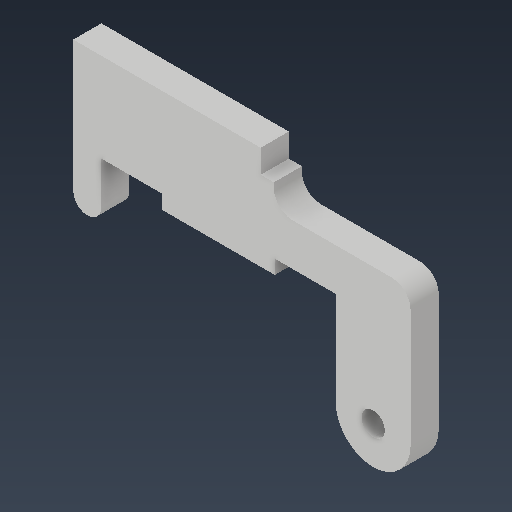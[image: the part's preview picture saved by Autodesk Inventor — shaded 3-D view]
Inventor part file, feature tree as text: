
AUTODESK INVENTOR PART (.ipt)
format: ipt  version: 2021 (Build 250183000, 183)  size: 145,920 bytes
history: native  units: mm
features: other x4, extrude x3, sketch x3, fillet x2, reference x1, projected_geometry x1
ambient origin geometry x8: Origin, YZ Plane, XZ Plane, XY Plane, X Axis, Y Axis, Z Axis, Center Point
bodies: Body1 (feature_tree)
feature tree (14):
  extrude  "Выдавливание2"  Depth=2.5mm
  extrude  "Выдавливание3"  Depth=3.0mm TaperAngle=0.0deg
  fillet  "Сопряжение3"  Radius=1.0mm
  fillet  "Сопряжение4"  Radius=2.0mm
  sketch  "Эскиз5"
  other  "РабПлоскость1"
  extrude  "Выдавливание4"  Depth=1.5mm
  sketch  "Эскиз1"
  reference  "Ссылка1"
  sketch  "Эскиз2"
  projected_geometry  "Спроецированная петля1"
  other  "<userpath>\Documents\GitHub\Tesla_coil_V1\3dModels\TeslaCoil.iam"
  other  "TeslaCoil.iam"
  other  "TopBox:1"
